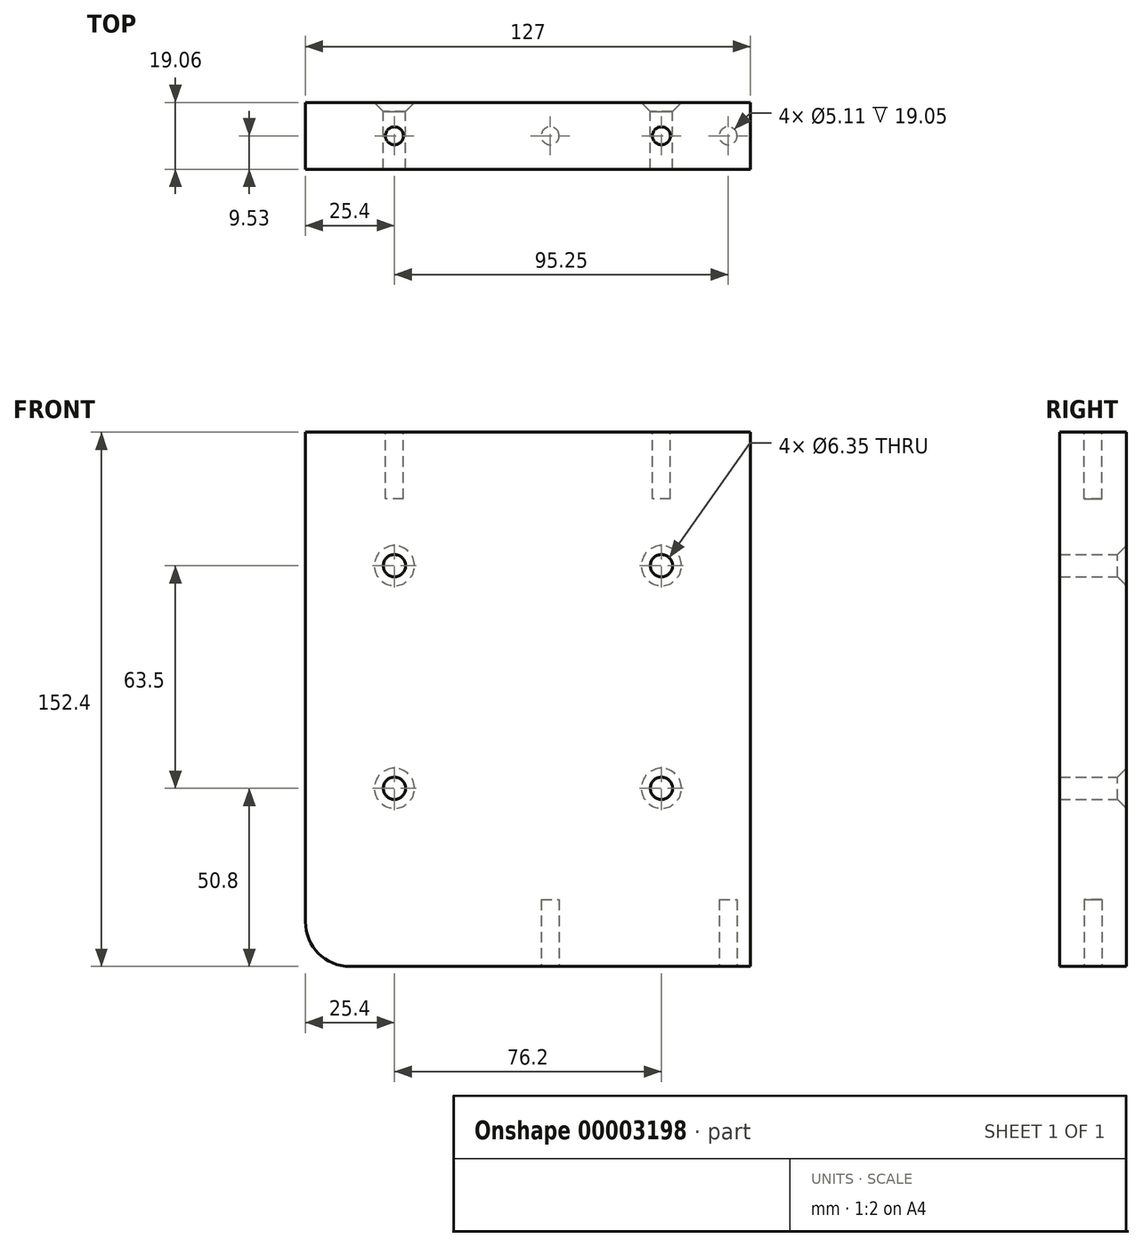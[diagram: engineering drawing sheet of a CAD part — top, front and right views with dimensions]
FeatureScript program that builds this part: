
annotation { "Feature Type Name" : "Feature", "Feature Type Description" : "" }
export const myFeature = defineFeature(function(context is Context, id is Id, definition is map)
    precondition{}
    {
        {
            var Q0;
            Q0=qCreatedBy(makeId("Front.planeOp"),FACE);
            var sketch = newSketch(context, id + "F0", { "sketchPlane" : qUnion([Q0])});
            skLineSegment(sketch, "E0", {"start": v(0, 0) * mm, "end": v(0, -152.4) * mm});
            skLineSegment(sketch, "E1", {"start": v(0, -152.4) * mm, "end": v(127, -152.4) * mm});
            skLineSegment(sketch, "E2", {"start": v(127, -152.4) * mm, "end": v(127, 0) * mm});
            skLineSegment(sketch, "E3", {"start": v(127, 0) * mm, "end": v(0, 0) * mm});
            skLineSegment(sketch, "E4", {"start": v(25.4, 0) * mm, "end": v(25.4, -152.4) * mm, "construction": true});
            skLineSegment(sketch, "E5", {"start": v(101.6, 0) * mm, "end": v(101.6, -152.4) * mm, "construction": true});
            skLineSegment(sketch, "E6", {"start": v(0, -38.1) * mm, "end": v(127, -38.1) * mm, "construction": true});
            skLineSegment(sketch, "E7", {"start": v(0, -101.6) * mm, "end": v(127, -101.6) * mm, "construction": true});
            skCircle(sketch, "E8", {"center": v(25.4, -38.1) * mm, "radius": 3.18 * mm});
            skCircle(sketch, "E9", {"center": v(101.6, -38.1) * mm, "radius": 3.18 * mm});
            skCircle(sketch, "E10", {"center": v(25.4, -101.6) * mm, "radius": 3.18 * mm});
            skCircle(sketch, "E11", {"center": v(101.6, -101.6) * mm, "radius": 3.18 * mm});
            skSolve(sketch);
        }
        {
            var Q0;
            Q0 = qSketchRegion(id + "F0", true);
            extrude(context, id + "F1", {"entities" : qUnion([Q0]), "endBound" : BoundingType.SYMMETRIC, "depth" : 19.05 * mm});
        }
        {
            var Q0;
            Q0=makeQuery(id+"F1.opExtrude","SWEPT_FACE",FACE,{"disambiguationData":[OSD([sQuery(id+"F0.wireOp",EDGE,"E1")])]});
            var sketch = newSketch(context, id + "F2", { "sketchPlane" : qUnion([Q0])});
            skLineSegment(sketch, "E12", {"start": v(0, 0) * mm, "end": v(127, 0) * mm, "construction": true});
            skLineSegment(sketch, "E13", {"start": v(69.85, 9.53) * mm, "end": v(69.85, -9.53) * mm, "construction": true});
            skLineSegment(sketch, "E14", {"start": v(120.65, 9.53) * mm, "end": v(120.65, -9.53) * mm, "construction": true});
            skCircle(sketch, "E15", {"center": v(120.65, 0) * mm, "radius": 2.55 * mm});
            skCircle(sketch, "E16", {"center": v(69.85, 0) * mm, "radius": 2.55 * mm});
            skSolve(sketch);
        }
        {
            var Q0;
            Q0 = qSketchRegion(id + "F2", true);
            extrude(context, id + "F3", {"entities" : qUnion([Q0]), "operationType" : NewBodyOperationType.REMOVE, "oppositeDirection" : true, "depth" : 19.05 * mm});
        }
        {
            var Q0;
            Q0=makeQuery(id+"F1.opExtrude","SWEPT_FACE",FACE,{"disambiguationData":[OSD([sQuery(id+"F0.wireOp",EDGE,"E3")])]});
            var sketch = newSketch(context, id + "F4", { "sketchPlane" : qUnion([Q0])});
            skLineSegment(sketch, "E17", {"start": v(2.46, 0) * mm, "end": v(127, 0) * mm, "construction": true});
            skLineSegment(sketch, "E18", {"start": v(25.4, 9.52) * mm, "end": v(25.4, -9.53) * mm, "construction": true});
            skLineSegment(sketch, "E19", {"start": v(101.6, 9.53) * mm, "end": v(101.6, -9.53) * mm, "construction": true});
            skCircle(sketch, "E20", {"center": v(25.4, 0) * mm, "radius": 2.55 * mm});
            skCircle(sketch, "E21", {"center": v(101.6, 0) * mm, "radius": 2.55 * mm});
            skSolve(sketch);
        }
        {
            var Q0;
            Q0 = qSketchRegion(id + "F4", true);
            extrude(context, id + "F5", {"entities" : qUnion([Q0]), "operationType" : NewBodyOperationType.REMOVE, "oppositeDirection" : true, "depth" : 19.05 * mm});
        }
        {
            var Q0;
            Q0=makeQuery(id+"F1.opExtrude","CAP_EDGE",EDGE,{"disambiguationData":[OSD([sQuery(id+"F0.wireOp",EDGE,"E10")])],"isStart":true});
            var Q1;
            Q1=makeQuery(id+"F1.opExtrude","CAP_EDGE",EDGE,{"disambiguationData":[OSD([sQuery(id+"F0.wireOp",EDGE,"E11")])],"isStart":true});
            var Q2;
            Q2=makeQuery(id+"F1.opExtrude","CAP_EDGE",EDGE,{"disambiguationData":[OSD([sQuery(id+"F0.wireOp",EDGE,"E9")])],"isStart":true});
            var Q3;
            Q3=makeQuery(id+"F1.opExtrude","CAP_EDGE",EDGE,{"disambiguationData":[OSD([sQuery(id+"F0.wireOp",EDGE,"E8")])],"isStart":true});
            chamfer(context, id + "F6", {"entities" : qUnion([Q0, Q1, Q2, Q3]), "chamferType" : ChamferType.OFFSET_ANGLE, "width" : 2.54 * mm, "oppositeDirection" : false, "angle" : 45 * degree, "tangentPropagation" : true});
        }
        {
            var Q0;
            Q0=makeQuery(id+"F1.opExtrude","SWEPT_EDGE",EDGE,{"disambiguationData":[OSD([sQuery(id+"F0.wireOp",EDGE,"E0"),sQuery(id+"F0.wireOp",EDGE,"E1")])]});
            fillet(context, id + "F7", {"entities" : qUnion([Q0]), "radius" : 12.7 * mm, "tangentPropagation" : true, "allowEdgeOverflow" : false});
        }
    });
